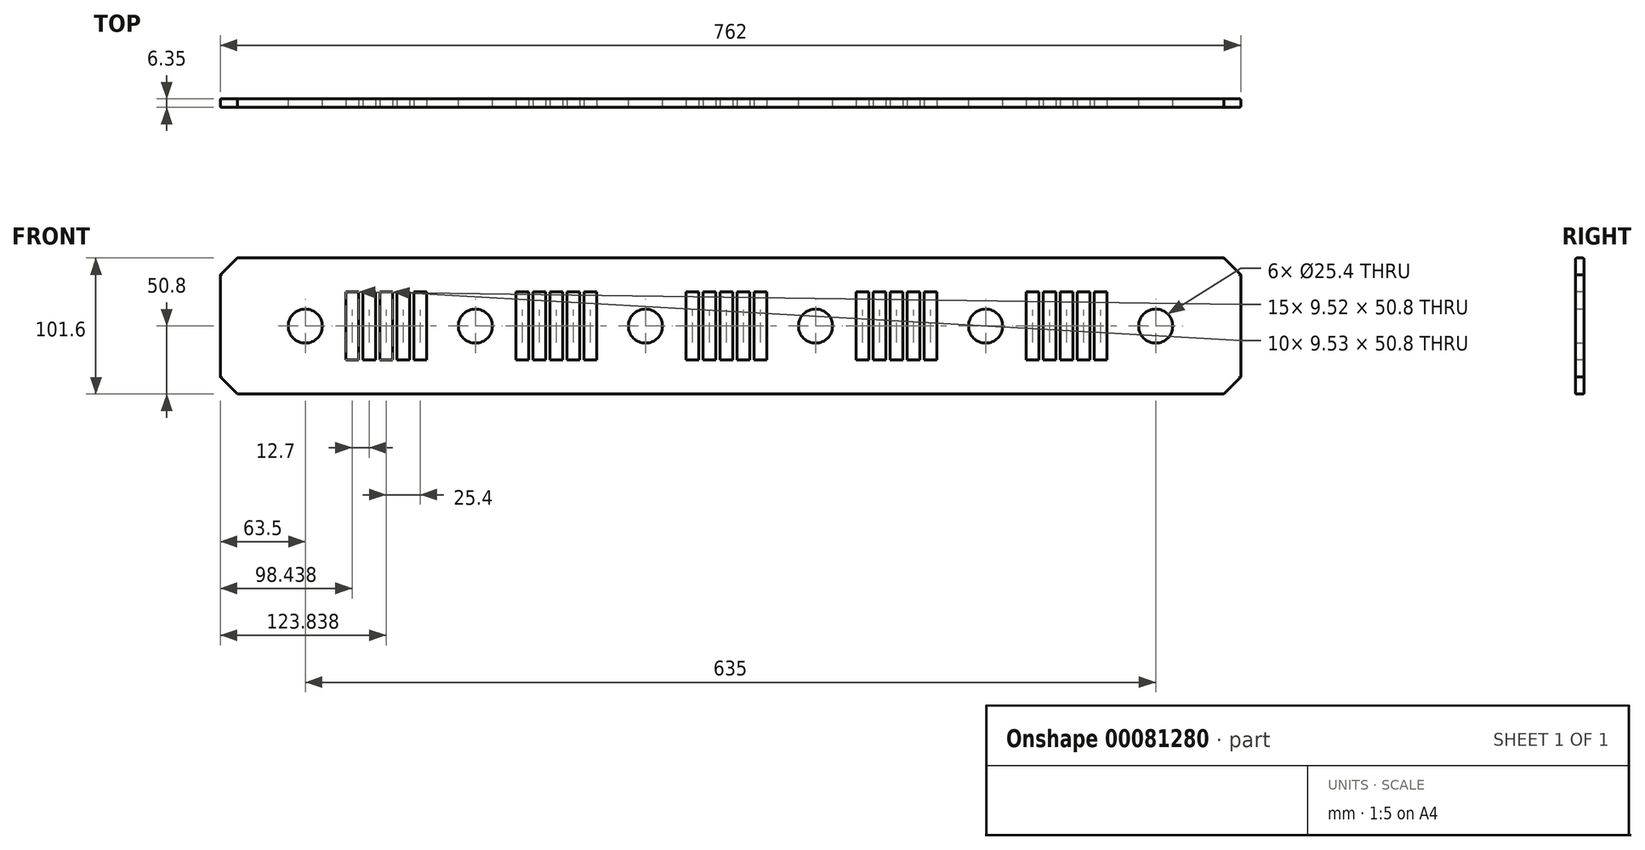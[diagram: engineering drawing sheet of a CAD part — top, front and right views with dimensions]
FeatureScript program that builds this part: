
annotation { "Feature Type Name" : "Feature", "Feature Type Description" : "" }
export const myFeature = defineFeature(function(context is Context, id is Id, definition is map)
    precondition{}
    {
        {
            var Q0;
            Q0=qCreatedBy(makeId("Front.planeOp"),FACE);
            var sketch = newSketch(context, id + "F0", { "sketchPlane" : qUnion([Q0])});
            skLineSegment(sketch, "E0.bottom", {"start": v(0, 0) * mm, "end": v(762, 0) * mm});
            skLineSegment(sketch, "E0.top", {"start": v(0, 101.6) * mm, "end": v(762, 101.6) * mm});
            skLineSegment(sketch, "E0.left", {"start": v(0, 0) * mm, "end": v(0, 101.6) * mm});
            skLineSegment(sketch, "E0.right", {"start": v(762, 0) * mm, "end": v(762, 101.6) * mm});
            skCircle(sketch, "E1", {"center": v(63.5, 50.8) * mm, "radius": 12.7 * mm});
            skPoint(sketch, "E1.centerSnap0", {"position": v(0, 50.8) * mm});
            skCircle(sketch, "E2", {"center": v(190.5, 50.8) * mm, "radius": 12.7 * mm});
            skCircle(sketch, "E3", {"center": v(317.5, 50.8) * mm, "radius": 12.7 * mm});
            skCircle(sketch, "E4", {"center": v(444.5, 50.8) * mm, "radius": 12.7 * mm});
            skCircle(sketch, "E5", {"center": v(571.5, 50.8) * mm, "radius": 12.7 * mm});
            skCircle(sketch, "E6", {"center": v(698.5, 50.8) * mm, "radius": 12.7 * mm});
            skSolve(sketch);
        }
        {
            var Q0;
            Q0 = qSketchRegion(id + "F0", true);
            extrude(context, id + "F1", {"entities" : qUnion([Q0]), "depth" : 6.35 * mm});
        }
        {
            var Q0;
            Q0=makeQuery(id+"F1.opExtrude","CAP_FACE",FACE,{"disambiguationData":[OSD([sQuery(id+"F0.wireOp",EDGE,"E0.bottom"),sQuery(id+"F0.wireOp",EDGE,"E0.top"),sQuery(id+"F0.wireOp",EDGE,"E0.left"),sQuery(id+"F0.wireOp",EDGE,"E0.right"),sQuery(id+"F0.wireOp",EDGE,"E1"),sQuery(id+"F0.wireOp",EDGE,"E2"),sQuery(id+"F0.wireOp",EDGE,"E3"),sQuery(id+"F0.wireOp",EDGE,"E4"),sQuery(id+"F0.wireOp",EDGE,"E5"),sQuery(id+"F0.wireOp",EDGE,"E6")])],"isStart":false});
            var sketch = newSketch(context, id + "F2", { "sketchPlane" : qUnion([Q0])});
            skLineSegment(sketch, "E7.bottom", {"start": v(93.68, 76.2) * mm, "end": v(103.2, 76.2) * mm});
            skLineSegment(sketch, "E7.top", {"start": v(93.68, 25.4) * mm, "end": v(103.2, 25.4) * mm});
            skLineSegment(sketch, "E7.left", {"start": v(93.68, 76.2) * mm, "end": v(93.68, 25.4) * mm});
            skLineSegment(sketch, "E7.right", {"start": v(103.2, 76.2) * mm, "end": v(103.2, 25.4) * mm});
            skLineSegment(sketch, "E8.1.0.0", {"start": v(106.38, 76.2) * mm, "end": v(115.9, 76.2) * mm});
            skLineSegment(sketch, "E8.1.0.1", {"start": v(106.38, 76.2) * mm, "end": v(106.38, 25.4) * mm});
            skLineSegment(sketch, "E8.1.0.2", {"start": v(106.38, 25.4) * mm, "end": v(115.9, 25.4) * mm});
            skLineSegment(sketch, "E8.1.0.3", {"start": v(115.9, 76.2) * mm, "end": v(115.9, 25.4) * mm});
            skLineSegment(sketch, "E8.2.0.0", {"start": v(119.08, 76.2) * mm, "end": v(128.6, 76.2) * mm});
            skLineSegment(sketch, "E8.2.0.1", {"start": v(119.08, 76.2) * mm, "end": v(119.08, 25.4) * mm});
            skLineSegment(sketch, "E8.2.0.2", {"start": v(119.08, 25.4) * mm, "end": v(128.6, 25.4) * mm});
            skLineSegment(sketch, "E8.2.0.3", {"start": v(128.6, 76.2) * mm, "end": v(128.6, 25.4) * mm});
            skLineSegment(sketch, "E8.3.0.0", {"start": v(131.78, 76.2) * mm, "end": v(141.3, 76.2) * mm});
            skLineSegment(sketch, "E8.3.0.1", {"start": v(131.78, 76.2) * mm, "end": v(131.78, 25.4) * mm});
            skLineSegment(sketch, "E8.3.0.2", {"start": v(131.78, 25.4) * mm, "end": v(141.3, 25.4) * mm});
            skLineSegment(sketch, "E8.3.0.3", {"start": v(141.3, 76.2) * mm, "end": v(141.3, 25.4) * mm});
            skLineSegment(sketch, "E8.4.0.0", {"start": v(144.48, 76.2) * mm, "end": v(154, 76.2) * mm});
            skLineSegment(sketch, "E8.4.0.1", {"start": v(144.48, 76.2) * mm, "end": v(144.48, 25.4) * mm});
            skLineSegment(sketch, "E8.4.0.2", {"start": v(144.48, 25.4) * mm, "end": v(154, 25.4) * mm});
            skLineSegment(sketch, "E8.4.0.3", {"start": v(154, 76.2) * mm, "end": v(154, 25.4) * mm});
            skLineSegment(sketch, "E8.direction1", {"start": v(93.68, 76.2) * mm, "end": v(106.38, 76.2) * mm, "construction": true});
            skLineSegment(sketch, "E9.bottom", {"start": v(220.68, 76.2) * mm, "end": v(230.2, 76.2) * mm});
            skLineSegment(sketch, "E9.top", {"start": v(220.68, 25.4) * mm, "end": v(230.2, 25.4) * mm});
            skLineSegment(sketch, "E9.left", {"start": v(220.68, 76.2) * mm, "end": v(220.68, 25.4) * mm});
            skLineSegment(sketch, "E9.right", {"start": v(230.2, 76.2) * mm, "end": v(230.2, 25.4) * mm});
            skLineSegment(sketch, "E10.1.0.0", {"start": v(233.38, 76.2) * mm, "end": v(242.9, 76.2) * mm});
            skLineSegment(sketch, "E10.1.0.1", {"start": v(233.38, 76.2) * mm, "end": v(233.38, 25.4) * mm});
            skLineSegment(sketch, "E10.1.0.2", {"start": v(233.38, 25.4) * mm, "end": v(242.9, 25.4) * mm});
            skLineSegment(sketch, "E10.1.0.3", {"start": v(242.9, 76.2) * mm, "end": v(242.9, 25.4) * mm});
            skLineSegment(sketch, "E10.2.0.0", {"start": v(246.08, 76.2) * mm, "end": v(255.6, 76.2) * mm});
            skLineSegment(sketch, "E10.2.0.1", {"start": v(246.08, 76.2) * mm, "end": v(246.08, 25.4) * mm});
            skLineSegment(sketch, "E10.2.0.2", {"start": v(246.08, 25.4) * mm, "end": v(255.6, 25.4) * mm});
            skLineSegment(sketch, "E10.2.0.3", {"start": v(255.6, 76.2) * mm, "end": v(255.6, 25.4) * mm});
            skLineSegment(sketch, "E10.3.0.0", {"start": v(258.78, 76.2) * mm, "end": v(268.3, 76.2) * mm});
            skLineSegment(sketch, "E10.3.0.1", {"start": v(258.78, 76.2) * mm, "end": v(258.78, 25.4) * mm});
            skLineSegment(sketch, "E10.3.0.2", {"start": v(258.78, 25.4) * mm, "end": v(268.3, 25.4) * mm});
            skLineSegment(sketch, "E10.3.0.3", {"start": v(268.3, 76.2) * mm, "end": v(268.3, 25.4) * mm});
            skLineSegment(sketch, "E10.4.0.0", {"start": v(271.48, 76.2) * mm, "end": v(281, 76.2) * mm});
            skLineSegment(sketch, "E10.4.0.1", {"start": v(271.48, 76.2) * mm, "end": v(271.48, 25.4) * mm});
            skLineSegment(sketch, "E10.4.0.2", {"start": v(271.48, 25.4) * mm, "end": v(281, 25.4) * mm});
            skLineSegment(sketch, "E10.4.0.3", {"start": v(281, 76.2) * mm, "end": v(281, 25.4) * mm});
            skLineSegment(sketch, "E10.direction1", {"start": v(220.68, 76.2) * mm, "end": v(233.38, 76.2) * mm, "construction": true});
            skLineSegment(sketch, "E11.bottom", {"start": v(347.68, 76.2) * mm, "end": v(357.2, 76.2) * mm});
            skLineSegment(sketch, "E11.top", {"start": v(347.68, 25.4) * mm, "end": v(357.2, 25.4) * mm});
            skLineSegment(sketch, "E11.left", {"start": v(347.68, 76.2) * mm, "end": v(347.68, 25.4) * mm});
            skLineSegment(sketch, "E11.right", {"start": v(357.2, 76.2) * mm, "end": v(357.2, 25.4) * mm});
            skLineSegment(sketch, "E12.1.0.0", {"start": v(360.38, 76.2) * mm, "end": v(369.9, 76.2) * mm});
            skLineSegment(sketch, "E12.1.0.1", {"start": v(360.38, 76.2) * mm, "end": v(360.38, 25.4) * mm});
            skLineSegment(sketch, "E12.1.0.2", {"start": v(360.38, 25.4) * mm, "end": v(369.9, 25.4) * mm});
            skLineSegment(sketch, "E12.1.0.3", {"start": v(369.9, 76.2) * mm, "end": v(369.9, 25.4) * mm});
            skLineSegment(sketch, "E12.2.0.0", {"start": v(373.08, 76.2) * mm, "end": v(382.6, 76.2) * mm});
            skLineSegment(sketch, "E12.2.0.1", {"start": v(373.08, 76.2) * mm, "end": v(373.08, 25.4) * mm});
            skLineSegment(sketch, "E12.2.0.2", {"start": v(373.08, 25.4) * mm, "end": v(382.6, 25.4) * mm});
            skLineSegment(sketch, "E12.2.0.3", {"start": v(382.6, 76.2) * mm, "end": v(382.6, 25.4) * mm});
            skLineSegment(sketch, "E12.3.0.0", {"start": v(385.78, 76.2) * mm, "end": v(395.3, 76.2) * mm});
            skLineSegment(sketch, "E12.3.0.1", {"start": v(385.78, 76.2) * mm, "end": v(385.78, 25.4) * mm});
            skLineSegment(sketch, "E12.3.0.2", {"start": v(385.78, 25.4) * mm, "end": v(395.3, 25.4) * mm});
            skLineSegment(sketch, "E12.3.0.3", {"start": v(395.3, 76.2) * mm, "end": v(395.3, 25.4) * mm});
            skLineSegment(sketch, "E12.4.0.0", {"start": v(398.48, 76.2) * mm, "end": v(408, 76.2) * mm});
            skLineSegment(sketch, "E12.4.0.1", {"start": v(398.48, 76.2) * mm, "end": v(398.48, 25.4) * mm});
            skLineSegment(sketch, "E12.4.0.2", {"start": v(398.48, 25.4) * mm, "end": v(408, 25.4) * mm});
            skLineSegment(sketch, "E12.4.0.3", {"start": v(408, 76.2) * mm, "end": v(408, 25.4) * mm});
            skLineSegment(sketch, "E12.direction1", {"start": v(347.68, 76.2) * mm, "end": v(360.38, 76.2) * mm, "construction": true});
            skLineSegment(sketch, "E13.bottom", {"start": v(474.68, 76.2) * mm, "end": v(484.2, 76.2) * mm});
            skLineSegment(sketch, "E13.top", {"start": v(474.68, 25.4) * mm, "end": v(484.2, 25.4) * mm});
            skLineSegment(sketch, "E13.left", {"start": v(474.68, 76.2) * mm, "end": v(474.68, 25.4) * mm});
            skLineSegment(sketch, "E13.right", {"start": v(484.2, 76.2) * mm, "end": v(484.2, 25.4) * mm});
            skLineSegment(sketch, "E14.1.0.0", {"start": v(487.38, 76.2) * mm, "end": v(496.9, 76.2) * mm});
            skLineSegment(sketch, "E14.1.0.1", {"start": v(487.38, 76.2) * mm, "end": v(487.38, 25.4) * mm});
            skLineSegment(sketch, "E14.1.0.2", {"start": v(487.38, 25.4) * mm, "end": v(496.9, 25.4) * mm});
            skLineSegment(sketch, "E14.1.0.3", {"start": v(496.9, 76.2) * mm, "end": v(496.9, 25.4) * mm});
            skLineSegment(sketch, "E14.2.0.0", {"start": v(500.08, 76.2) * mm, "end": v(509.6, 76.2) * mm});
            skLineSegment(sketch, "E14.2.0.1", {"start": v(500.08, 76.2) * mm, "end": v(500.08, 25.4) * mm});
            skLineSegment(sketch, "E14.2.0.2", {"start": v(500.08, 25.4) * mm, "end": v(509.6, 25.4) * mm});
            skLineSegment(sketch, "E14.2.0.3", {"start": v(509.6, 76.2) * mm, "end": v(509.6, 25.4) * mm});
            skLineSegment(sketch, "E14.3.0.0", {"start": v(512.78, 76.2) * mm, "end": v(522.3, 76.2) * mm});
            skLineSegment(sketch, "E14.3.0.1", {"start": v(512.78, 76.2) * mm, "end": v(512.78, 25.4) * mm});
            skLineSegment(sketch, "E14.3.0.2", {"start": v(512.78, 25.4) * mm, "end": v(522.3, 25.4) * mm});
            skLineSegment(sketch, "E14.3.0.3", {"start": v(522.3, 76.2) * mm, "end": v(522.3, 25.4) * mm});
            skLineSegment(sketch, "E14.4.0.0", {"start": v(525.48, 76.2) * mm, "end": v(535, 76.2) * mm});
            skLineSegment(sketch, "E14.4.0.1", {"start": v(525.48, 76.2) * mm, "end": v(525.48, 25.4) * mm});
            skLineSegment(sketch, "E14.4.0.2", {"start": v(525.48, 25.4) * mm, "end": v(535, 25.4) * mm});
            skLineSegment(sketch, "E14.4.0.3", {"start": v(535, 76.2) * mm, "end": v(535, 25.4) * mm});
            skLineSegment(sketch, "E14.direction1", {"start": v(474.68, 76.2) * mm, "end": v(487.38, 76.2) * mm, "construction": true});
            skLineSegment(sketch, "E15.bottom", {"start": v(601.68, 76.2) * mm, "end": v(611.2, 76.2) * mm});
            skLineSegment(sketch, "E15.top", {"start": v(601.68, 25.4) * mm, "end": v(611.2, 25.4) * mm});
            skLineSegment(sketch, "E15.left", {"start": v(601.68, 76.2) * mm, "end": v(601.68, 25.4) * mm});
            skLineSegment(sketch, "E15.right", {"start": v(611.2, 76.2) * mm, "end": v(611.2, 25.4) * mm});
            skLineSegment(sketch, "E16.1.0.0", {"start": v(614.38, 76.2) * mm, "end": v(623.9, 76.2) * mm});
            skLineSegment(sketch, "E16.1.0.1", {"start": v(614.38, 76.2) * mm, "end": v(614.38, 25.4) * mm});
            skLineSegment(sketch, "E16.1.0.2", {"start": v(614.38, 25.4) * mm, "end": v(623.9, 25.4) * mm});
            skLineSegment(sketch, "E16.1.0.3", {"start": v(623.9, 76.2) * mm, "end": v(623.9, 25.4) * mm});
            skLineSegment(sketch, "E16.2.0.0", {"start": v(627.08, 76.2) * mm, "end": v(636.6, 76.2) * mm});
            skLineSegment(sketch, "E16.2.0.1", {"start": v(627.08, 76.2) * mm, "end": v(627.08, 25.4) * mm});
            skLineSegment(sketch, "E16.2.0.2", {"start": v(627.08, 25.4) * mm, "end": v(636.6, 25.4) * mm});
            skLineSegment(sketch, "E16.2.0.3", {"start": v(636.6, 76.2) * mm, "end": v(636.6, 25.4) * mm});
            skLineSegment(sketch, "E16.3.0.0", {"start": v(639.78, 76.2) * mm, "end": v(649.3, 76.2) * mm});
            skLineSegment(sketch, "E16.3.0.1", {"start": v(639.78, 76.2) * mm, "end": v(639.78, 25.4) * mm});
            skLineSegment(sketch, "E16.3.0.2", {"start": v(639.78, 25.4) * mm, "end": v(649.3, 25.4) * mm});
            skLineSegment(sketch, "E16.3.0.3", {"start": v(649.3, 76.2) * mm, "end": v(649.3, 25.4) * mm});
            skLineSegment(sketch, "E16.4.0.0", {"start": v(652.48, 76.2) * mm, "end": v(662, 76.2) * mm});
            skLineSegment(sketch, "E16.4.0.1", {"start": v(652.48, 76.2) * mm, "end": v(652.48, 25.4) * mm});
            skLineSegment(sketch, "E16.4.0.2", {"start": v(652.48, 25.4) * mm, "end": v(662, 25.4) * mm});
            skLineSegment(sketch, "E16.4.0.3", {"start": v(662, 76.2) * mm, "end": v(662, 25.4) * mm});
            skLineSegment(sketch, "E16.direction1", {"start": v(601.68, 76.2) * mm, "end": v(614.38, 76.2) * mm, "construction": true});
            skSolve(sketch);
        }
        {
            var Q0;
            Q0 = qSketchRegion(id + "F2", true);
            extrude(context, id + "F3", {"entities" : qUnion([Q0]), "operationType" : NewBodyOperationType.REMOVE, "oppositeDirection" : true, "depth" : 25.4 * mm});
        }
        {
            var Q0;
            Q0=makeQuery(id+"F1.opExtrude","SWEPT_EDGE",EDGE,{"disambiguationData":[OSD([sQuery(id+"F0.wireOp",EDGE,"E0.top"),sQuery(id+"F0.wireOp",EDGE,"E0.right")])]});
            var Q1;
            Q1=makeQuery(id+"F1.opExtrude","SWEPT_EDGE",EDGE,{"disambiguationData":[OSD([sQuery(id+"F0.wireOp",EDGE,"E0.bottom"),sQuery(id+"F0.wireOp",EDGE,"E0.right")])]});
            var Q2;
            Q2=makeQuery(id+"F1.opExtrude","SWEPT_EDGE",EDGE,{"disambiguationData":[OSD([sQuery(id+"F0.wireOp",EDGE,"E0.bottom"),sQuery(id+"F0.wireOp",EDGE,"E0.left")])]});
            var Q3;
            Q3=makeQuery(id+"F1.opExtrude","SWEPT_EDGE",EDGE,{"disambiguationData":[OSD([sQuery(id+"F0.wireOp",EDGE,"E0.top"),sQuery(id+"F0.wireOp",EDGE,"E0.left")])]});
            chamfer(context, id + "F4", {"entities" : qUnion([Q0, Q1, Q2, Q3]), "width" : 12.7 * mm, "tangentPropagation" : true});
        }
        {
            var Q0;
            {var subQ0=sQuery(id+"F0.wireOp",EDGE,"E0.left");var subQ1=sQuery(id+"F0.wireOp",EDGE,"E0.top");Q0=makeQuery(id+"F4.opChamfer","BLEND_EDGE",EDGE,{"blendedFrom":[makeQuery(id+"F1.opExtrude","SWEPT_EDGE",EDGE,{"disambiguationData":[OSD([subQ1,subQ0])]}),makeQuery(id+"F1.opExtrude","CAP_FACE",FACE,{"disambiguationData":[OSD([sQuery(id+"F0.wireOp",EDGE,"E0.bottom"),subQ1,subQ0,sQuery(id+"F0.wireOp",EDGE,"E0.right"),sQuery(id+"F0.wireOp",EDGE,"E1"),sQuery(id+"F0.wireOp",EDGE,"E2"),sQuery(id+"F0.wireOp",EDGE,"E3"),sQuery(id+"F0.wireOp",EDGE,"E4"),sQuery(id+"F0.wireOp",EDGE,"E5"),sQuery(id+"F0.wireOp",EDGE,"E6")])],"isStart":false})],"blendedInto":[makeQuery(id+"F1.opExtrude","CAP_FACE",FACE,{"disambiguationData":[OSD([sQuery(id+"F0.wireOp",EDGE,"E0.bottom"),subQ1,subQ0,sQuery(id+"F0.wireOp",EDGE,"E0.right"),sQuery(id+"F0.wireOp",EDGE,"E1"),sQuery(id+"F0.wireOp",EDGE,"E2"),sQuery(id+"F0.wireOp",EDGE,"E3"),sQuery(id+"F0.wireOp",EDGE,"E4"),sQuery(id+"F0.wireOp",EDGE,"E5"),sQuery(id+"F0.wireOp",EDGE,"E6")])],"isStart":false})]});}
            var Q1;
            Q1=makeQuery(id+"F1.opExtrude","CAP_EDGE",EDGE,{"disambiguationData":[OSD([sQuery(id+"F0.wireOp",EDGE,"E0.top")])],"isStart":false});
            var Q2;
            Q2=makeQuery(id+"F1.opExtrude","CAP_EDGE",EDGE,{"disambiguationData":[OSD([sQuery(id+"F0.wireOp",EDGE,"E0.left")])],"isStart":true});
            var Q3;
            Q3=makeQuery(id+"F1.opExtrude","CAP_EDGE",EDGE,{"disambiguationData":[OSD([sQuery(id+"F0.wireOp",EDGE,"E0.bottom")])],"isStart":false});
            var Q4;
            {var subQ0=sQuery(id+"F0.wireOp",EDGE,"E0.left");var subQ1=sQuery(id+"F0.wireOp",EDGE,"E0.bottom");Q4=makeQuery(id+"F4.opChamfer","BLEND_EDGE",EDGE,{"blendedFrom":[makeQuery(id+"F1.opExtrude","SWEPT_EDGE",EDGE,{"disambiguationData":[OSD([subQ1,subQ0])]}),makeQuery(id+"F1.opExtrude","CAP_FACE",FACE,{"disambiguationData":[OSD([subQ1,sQuery(id+"F0.wireOp",EDGE,"E0.top"),subQ0,sQuery(id+"F0.wireOp",EDGE,"E0.right"),sQuery(id+"F0.wireOp",EDGE,"E1"),sQuery(id+"F0.wireOp",EDGE,"E2"),sQuery(id+"F0.wireOp",EDGE,"E3"),sQuery(id+"F0.wireOp",EDGE,"E4"),sQuery(id+"F0.wireOp",EDGE,"E5"),sQuery(id+"F0.wireOp",EDGE,"E6")])],"isStart":false})],"blendedInto":[makeQuery(id+"F1.opExtrude","CAP_FACE",FACE,{"disambiguationData":[OSD([subQ1,sQuery(id+"F0.wireOp",EDGE,"E0.top"),subQ0,sQuery(id+"F0.wireOp",EDGE,"E0.right"),sQuery(id+"F0.wireOp",EDGE,"E1"),sQuery(id+"F0.wireOp",EDGE,"E2"),sQuery(id+"F0.wireOp",EDGE,"E3"),sQuery(id+"F0.wireOp",EDGE,"E4"),sQuery(id+"F0.wireOp",EDGE,"E5"),sQuery(id+"F0.wireOp",EDGE,"E6")])],"isStart":false})]});}
            var Q5;
            {var subQ0=sQuery(id+"F0.wireOp",EDGE,"E0.right");var subQ1=sQuery(id+"F0.wireOp",EDGE,"E0.top");Q5=makeQuery(id+"F4.opChamfer","BLEND_EDGE",EDGE,{"blendedFrom":[makeQuery(id+"F1.opExtrude","SWEPT_EDGE",EDGE,{"disambiguationData":[OSD([subQ1,subQ0])]}),makeQuery(id+"F1.opExtrude","CAP_FACE",FACE,{"disambiguationData":[OSD([sQuery(id+"F0.wireOp",EDGE,"E0.bottom"),subQ1,sQuery(id+"F0.wireOp",EDGE,"E0.left"),subQ0,sQuery(id+"F0.wireOp",EDGE,"E1"),sQuery(id+"F0.wireOp",EDGE,"E2"),sQuery(id+"F0.wireOp",EDGE,"E3"),sQuery(id+"F0.wireOp",EDGE,"E4"),sQuery(id+"F0.wireOp",EDGE,"E5"),sQuery(id+"F0.wireOp",EDGE,"E6")])],"isStart":false})],"blendedInto":[makeQuery(id+"F1.opExtrude","CAP_FACE",FACE,{"disambiguationData":[OSD([sQuery(id+"F0.wireOp",EDGE,"E0.bottom"),subQ1,sQuery(id+"F0.wireOp",EDGE,"E0.left"),subQ0,sQuery(id+"F0.wireOp",EDGE,"E1"),sQuery(id+"F0.wireOp",EDGE,"E2"),sQuery(id+"F0.wireOp",EDGE,"E3"),sQuery(id+"F0.wireOp",EDGE,"E4"),sQuery(id+"F0.wireOp",EDGE,"E5"),sQuery(id+"F0.wireOp",EDGE,"E6")])],"isStart":false})]});}
            var Q6;
            {var subQ0=sQuery(id+"F0.wireOp",EDGE,"E0.right");var subQ1=sQuery(id+"F0.wireOp",EDGE,"E0.bottom");Q6=makeQuery(id+"F4.opChamfer","BLEND_EDGE",EDGE,{"blendedFrom":[makeQuery(id+"F1.opExtrude","SWEPT_EDGE",EDGE,{"disambiguationData":[OSD([subQ1,subQ0])]}),makeQuery(id+"F1.opExtrude","CAP_FACE",FACE,{"disambiguationData":[OSD([subQ1,sQuery(id+"F0.wireOp",EDGE,"E0.top"),sQuery(id+"F0.wireOp",EDGE,"E0.left"),subQ0,sQuery(id+"F0.wireOp",EDGE,"E1"),sQuery(id+"F0.wireOp",EDGE,"E2"),sQuery(id+"F0.wireOp",EDGE,"E3"),sQuery(id+"F0.wireOp",EDGE,"E4"),sQuery(id+"F0.wireOp",EDGE,"E5"),sQuery(id+"F0.wireOp",EDGE,"E6")])],"isStart":false})],"blendedInto":[makeQuery(id+"F1.opExtrude","CAP_FACE",FACE,{"disambiguationData":[OSD([subQ1,sQuery(id+"F0.wireOp",EDGE,"E0.top"),sQuery(id+"F0.wireOp",EDGE,"E0.left"),subQ0,sQuery(id+"F0.wireOp",EDGE,"E1"),sQuery(id+"F0.wireOp",EDGE,"E2"),sQuery(id+"F0.wireOp",EDGE,"E3"),sQuery(id+"F0.wireOp",EDGE,"E4"),sQuery(id+"F0.wireOp",EDGE,"E5"),sQuery(id+"F0.wireOp",EDGE,"E6")])],"isStart":false})]});}
            var Q7;
            Q7=makeQuery(id+"F1.opExtrude","CAP_EDGE",EDGE,{"disambiguationData":[OSD([sQuery(id+"F0.wireOp",EDGE,"E0.right")])],"isStart":false});
            var Q8;
            Q8=makeQuery(id+"F1.opExtrude","CAP_EDGE",EDGE,{"disambiguationData":[OSD([sQuery(id+"F0.wireOp",EDGE,"E0.top")])],"isStart":true});
            var Q9;
            {var subQ0=sQuery(id+"F0.wireOp",EDGE,"E0.left");var subQ1=sQuery(id+"F0.wireOp",EDGE,"E0.top");Q9=makeQuery(id+"F4.opChamfer","BLEND_EDGE",EDGE,{"blendedFrom":[makeQuery(id+"F1.opExtrude","SWEPT_EDGE",EDGE,{"disambiguationData":[OSD([subQ1,subQ0])]}),makeQuery(id+"F1.opExtrude","CAP_FACE",FACE,{"disambiguationData":[OSD([sQuery(id+"F0.wireOp",EDGE,"E0.bottom"),subQ1,subQ0,sQuery(id+"F0.wireOp",EDGE,"E0.right"),sQuery(id+"F0.wireOp",EDGE,"E1"),sQuery(id+"F0.wireOp",EDGE,"E2"),sQuery(id+"F0.wireOp",EDGE,"E3"),sQuery(id+"F0.wireOp",EDGE,"E4"),sQuery(id+"F0.wireOp",EDGE,"E5"),sQuery(id+"F0.wireOp",EDGE,"E6")])],"isStart":true})],"blendedInto":[makeQuery(id+"F1.opExtrude","CAP_FACE",FACE,{"disambiguationData":[OSD([sQuery(id+"F0.wireOp",EDGE,"E0.bottom"),subQ1,subQ0,sQuery(id+"F0.wireOp",EDGE,"E0.right"),sQuery(id+"F0.wireOp",EDGE,"E1"),sQuery(id+"F0.wireOp",EDGE,"E2"),sQuery(id+"F0.wireOp",EDGE,"E3"),sQuery(id+"F0.wireOp",EDGE,"E4"),sQuery(id+"F0.wireOp",EDGE,"E5"),sQuery(id+"F0.wireOp",EDGE,"E6")])],"isStart":true})]});}
            var Q10;
            Q10=makeQuery(id+"F1.opExtrude","CAP_EDGE",EDGE,{"disambiguationData":[OSD([sQuery(id+"F0.wireOp",EDGE,"E0.left")])],"isStart":false});
            var Q11;
            {var subQ0=sQuery(id+"F0.wireOp",EDGE,"E0.left");var subQ1=sQuery(id+"F0.wireOp",EDGE,"E0.bottom");Q11=makeQuery(id+"F4.opChamfer","BLEND_EDGE",EDGE,{"blendedFrom":[makeQuery(id+"F1.opExtrude","SWEPT_EDGE",EDGE,{"disambiguationData":[OSD([subQ1,subQ0])]}),makeQuery(id+"F1.opExtrude","CAP_FACE",FACE,{"disambiguationData":[OSD([subQ1,sQuery(id+"F0.wireOp",EDGE,"E0.top"),subQ0,sQuery(id+"F0.wireOp",EDGE,"E0.right"),sQuery(id+"F0.wireOp",EDGE,"E1"),sQuery(id+"F0.wireOp",EDGE,"E2"),sQuery(id+"F0.wireOp",EDGE,"E3"),sQuery(id+"F0.wireOp",EDGE,"E4"),sQuery(id+"F0.wireOp",EDGE,"E5"),sQuery(id+"F0.wireOp",EDGE,"E6")])],"isStart":true})],"blendedInto":[makeQuery(id+"F1.opExtrude","CAP_FACE",FACE,{"disambiguationData":[OSD([subQ1,sQuery(id+"F0.wireOp",EDGE,"E0.top"),subQ0,sQuery(id+"F0.wireOp",EDGE,"E0.right"),sQuery(id+"F0.wireOp",EDGE,"E1"),sQuery(id+"F0.wireOp",EDGE,"E2"),sQuery(id+"F0.wireOp",EDGE,"E3"),sQuery(id+"F0.wireOp",EDGE,"E4"),sQuery(id+"F0.wireOp",EDGE,"E5"),sQuery(id+"F0.wireOp",EDGE,"E6")])],"isStart":true})]});}
            var Q12;
            Q12=makeQuery(id+"F1.opExtrude","CAP_EDGE",EDGE,{"disambiguationData":[OSD([sQuery(id+"F0.wireOp",EDGE,"E0.bottom")])],"isStart":true});
            var Q13;
            {var subQ0=sQuery(id+"F0.wireOp",EDGE,"E0.right");var subQ1=sQuery(id+"F0.wireOp",EDGE,"E0.bottom");Q13=makeQuery(id+"F4.opChamfer","BLEND_EDGE",EDGE,{"blendedFrom":[makeQuery(id+"F1.opExtrude","SWEPT_EDGE",EDGE,{"disambiguationData":[OSD([subQ1,subQ0])]}),makeQuery(id+"F1.opExtrude","CAP_FACE",FACE,{"disambiguationData":[OSD([subQ1,sQuery(id+"F0.wireOp",EDGE,"E0.top"),sQuery(id+"F0.wireOp",EDGE,"E0.left"),subQ0,sQuery(id+"F0.wireOp",EDGE,"E1"),sQuery(id+"F0.wireOp",EDGE,"E2"),sQuery(id+"F0.wireOp",EDGE,"E3"),sQuery(id+"F0.wireOp",EDGE,"E4"),sQuery(id+"F0.wireOp",EDGE,"E5"),sQuery(id+"F0.wireOp",EDGE,"E6")])],"isStart":true})],"blendedInto":[makeQuery(id+"F1.opExtrude","CAP_FACE",FACE,{"disambiguationData":[OSD([subQ1,sQuery(id+"F0.wireOp",EDGE,"E0.top"),sQuery(id+"F0.wireOp",EDGE,"E0.left"),subQ0,sQuery(id+"F0.wireOp",EDGE,"E1"),sQuery(id+"F0.wireOp",EDGE,"E2"),sQuery(id+"F0.wireOp",EDGE,"E3"),sQuery(id+"F0.wireOp",EDGE,"E4"),sQuery(id+"F0.wireOp",EDGE,"E5"),sQuery(id+"F0.wireOp",EDGE,"E6")])],"isStart":true})]});}
            var Q14;
            Q14=makeQuery(id+"F1.opExtrude","CAP_EDGE",EDGE,{"disambiguationData":[OSD([sQuery(id+"F0.wireOp",EDGE,"E0.right")])],"isStart":true});
            fillet(context, id + "F5", {"entities" : qUnion([Q0, Q1, Q2, Q3, Q4, Q5, Q6, Q7, Q8, Q9, Q10, Q11, Q12, Q13, Q14]), "radius" : 0.91 * mm, "tangentPropagation" : true, "allowEdgeOverflow" : false});
        }
    });
